# Revit family: 2CKA002011A6242
name_source: partatom
category: Elektroinstallationen
revit_build: Autodesk Revit 2017 (Build: 20160225_1515(x64)
units: mm (PartAtom-declared; Revit-internal decimal feet)

## family parameters
Basisbauteil = Fläche
Beim Laden mit Abzugskörper schneiden = Nein
Bemaßung runder Anschluss = Durchmesser verwenden
Beschriftungsausrichtung beibehalten = Nein
Gemeinsam genutzt = Nein
Raumberechnungspunkt = Nein
Teiletyp = Normal

## types (1)
- 2CKA002011A6242
    Abschließbar = Nein
    Anschlussart = Steckklemme
    Anzahl der Einheiten = 1
    Aufdruck/Kennzeichnung = ohne Aufdruck
    Ausführung = Schuko
    Ausführung der Oberfläche = glänzend
    Auswurfmechanismus = Nein
    BIM = https://media.live.bim.site
    BIMSITE_PRODUCT_ID = 12ec52b81e66956537b2850e6fab3ebd2a7ef7d6
    Befestigungsart = Krallen-/Schraubbefestigung
    Beschreibung = SCHUKO Unterputz-Steckdose, alpinweiß, Busch-balance SI, Steckdosen, SCHUKO Unterputz-Steckdose Mit Steckanschluss. 2-polig (2 P + E) Komplettabdeckung. Nennstrom: 16 A
    Datenblatt = https://media.live.bim.site
    Farbe = weiß
    Fehlerstromschutz = Nein
    Frequenz [Hz] = [50:50]
    GTIN = 4011395191323
    Geeignet für Schutzart (IP) = IP20
    Gerätebreite [mm] = 91
    Gerätehöhe [mm] = 91
    Gerätetiefe [mm] = 41
    Gewicht [kg/m] = 0.107
    HAN = 2CKA002011A6242
    Halogenfrei = Ja
    HeinzeBIM = https://www.heinze.de
    Hersteller = Busch-Jaeger
    Ist System = Nein
    Ist Zubehör = Nein
    Mit Klappdeckel = Nein
    Mit erhöhtem Berührungsschutz = Nein
    Montageart = Unterputz
    Nennspannung [V] [Volt] = 250
    Nennstrom = 16 A
    Oberfläche = unbehandelt
    Produktseite = https://media.live.bim.site
    RAL-Nummer (ähnlich) = 9010
    Sonderstromversorgung = sonstige
    TYPE = 20 EUJ-914
    Textfeld/Beschriftungsfläche = Nein
    Typname = SCHUKO Unterputz-Steckdose, alpinweiß, Busch-balance SI, Steckdosen
    URL = https://www.busch-jaeger.de
    Verdrehter Zentraleinsatz = Nein
    Vorgabe-Ansicht = 1219 mm
    Werkstoff = Kunststoff
    Werkstoffgüte = Thermoplast
    Überspannungsschutz = Nein

## geometry (parser evidence)
native form markers: Sweep x6
no freeform markers — native parametric forms only
